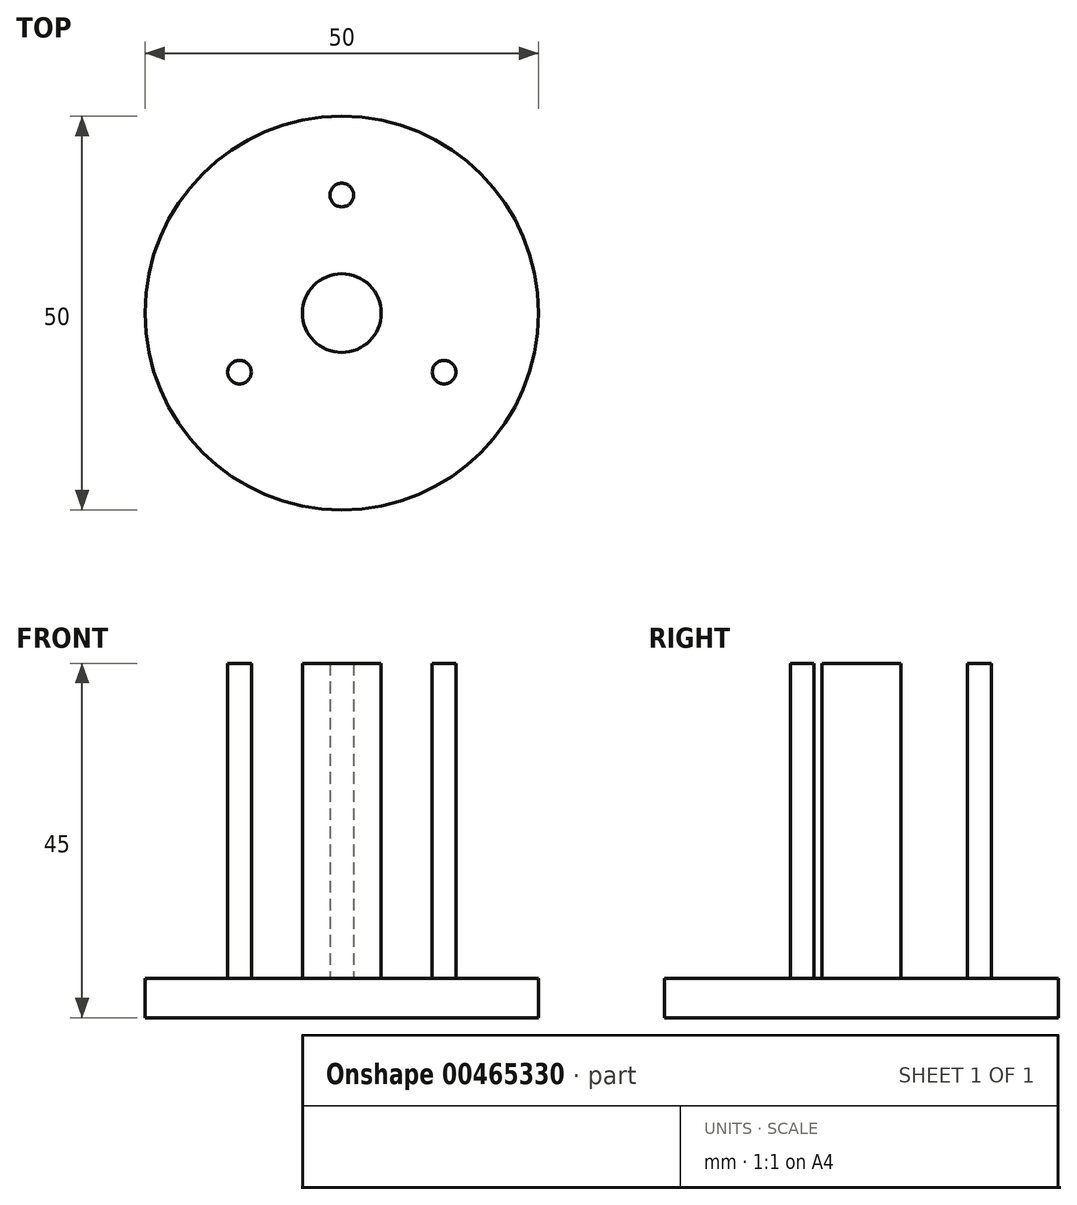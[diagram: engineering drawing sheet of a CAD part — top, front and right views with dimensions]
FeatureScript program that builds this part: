
annotation { "Feature Type Name" : "Feature", "Feature Type Description" : "" }
export const myFeature = defineFeature(function(context is Context, id is Id, definition is map)
    precondition{}
    {
        {
            var Q0;
            Q0=qCreatedBy(makeId("Top.planeOp"),FACE);
            var sketch = newSketch(context, id + "F0", { "sketchPlane" : qUnion([Q0])});
            skCircle(sketch, "E0", {"center": v(0, 0) * mm, "radius": 25 * mm});
            skSolve(sketch);
        }
        {
            var Q0;
            Q0=makeQuery(id+"F0.imprint","IMPRINT",FACE,{"disambiguationData":[TD([[makeQuery(id+"F0.imprint","IMPRINT",EDGE,{"derivedFrom":sQuery(id+"F0.wireOp",EDGE,"E0")}),1.0]])]});
            extrude(context, id + "F1", {"entities" : qUnion([Q0]), "depth" : 5 * mm});
        }
        {
            var Q0;
            Q0=makeQuery(id+"F1.opExtrude","CAP_FACE",FACE,{"disambiguationData":[OSD([sQuery(id+"F0.wireOp",EDGE,"E0")])],"isStart":false});
            var sketch = newSketch(context, id + "F2", { "sketchPlane" : qUnion([Q0])});
            skCircle(sketch, "E1", {"center": v(0, 0) * mm, "radius": 5 * mm});
            skSolve(sketch);
        }
        {
            var Q0;
            Q0=makeQuery(id+"F2.imprint","IMPRINT",FACE,{"disambiguationData":[TD([[makeQuery(id+"F2.imprint","IMPRINT",EDGE,{"derivedFrom":sQuery(id+"F2.wireOp",EDGE,"E1")}),1.0]])]});
            extrude(context, id + "F3", {"entities" : qUnion([Q0]), "operationType" : NewBodyOperationType.ADD, "depth" : 40 * mm});
        }
        {
            var Q0;
            Q0=makeQuery(id+"F1.opExtrude","CAP_FACE",FACE,{"disambiguationData":[OSD([sQuery(id+"F0.wireOp",EDGE,"E0")])],"isStart":false});
            var sketch = newSketch(context, id + "F4", { "sketchPlane" : qUnion([Q0])});
            skCircle(sketch, "E2", {"center": v(0, 0) * mm, "radius": 10 * mm});
            skCircle(sketch, "E3", {"center": v(0, 0) * mm, "radius": 6 * mm});
            skSolve(sketch);
        }
        {
            var Q0;
            {var subQ0=sQuery(id+"F0.wireOp",EDGE,"E0");Q0=makeQuery(id+"FdKcscAgNhMZup8_1.boolean.opBoolean","SPLIT",FACE,{"disambiguationData":[TD([makeQuery(id+"F1.opExtrude","SWEPT_FACE",FACE,{"disambiguationData":[OSD([subQ0])]})])],"derivedFrom":makeQuery(id+"F1.opExtrude","CAP_FACE",FACE,{"disambiguationData":[OSD([subQ0])],"isStart":false})});}
            var sketch = newSketch(context, id + "F5", { "sketchPlane" : qUnion([Q0])});
            skCircle(sketch, "E4.cCircle", {"center": v(0, 0) * mm, "radius": 15 * mm, "construction": true});
            skLineSegment(sketch, "E4.0", {"start": v(0, 15) * mm, "end": v(13, -7.5) * mm, "construction": true});
            skLineSegment(sketch, "E4.1", {"start": v(13, -7.5) * mm, "end": v(-13, -7.5) * mm, "construction": true});
            skLineSegment(sketch, "E4.2", {"start": v(-13, -7.5) * mm, "end": v(0, 15) * mm, "construction": true});
            skCircle(sketch, "E5", {"center": v(0, 15) * mm, "radius": 1.5 * mm});
            skCircle(sketch, "E6", {"center": v(13, -7.5) * mm, "radius": 1.5 * mm});
            skCircle(sketch, "E7", {"center": v(-13, -7.5) * mm, "radius": 1.5 * mm});
            skSolve(sketch);
        }
        {
            var Q0;
            Q0 = qSketchRegion(id + "F5", true);
            extrude(context, id + "F6", {"entities" : qUnion([Q0]), "operationType" : NewBodyOperationType.ADD, "depth" : 40 * mm});
        }
    });
